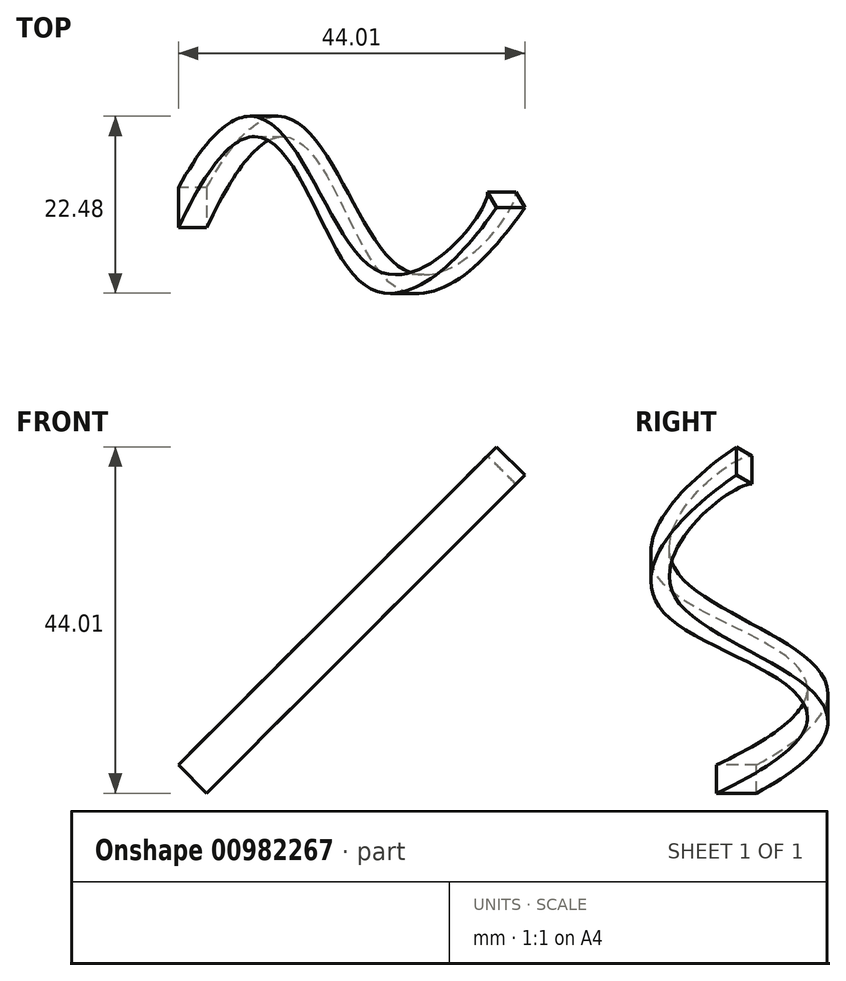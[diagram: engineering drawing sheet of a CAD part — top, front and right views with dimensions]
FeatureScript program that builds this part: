
annotation { "Feature Type Name" : "Feature", "Feature Type Description" : "" }
export const myFeature = defineFeature(function(context is Context, id is Id, definition is map)
    precondition{}
    {
        {
            var Q0;
            Q0=qCreatedBy(makeId("Front.planeOp"),FACE);
            var sketch = newSketch(context, id + "F0", { "sketchPlane" : qUnion([Q0])});
            skLineSegment(sketch, "E0", {"start": v(0, 0) * mm, "end": v(27, 27) * mm, "construction": true});
            skSolve(sketch);
        }
        {
            var Q0;
            Q0=qCreatedBy(makeId("Top.planeOp"),FACE);
            var Q1;
            Q1=sQuery(id+"F0.wireOp",EDGE,"E0");
            cPlane(context, id + "F1", {"entities" : qUnion([Q0, Q1]), "cplaneType" : CPlaneType.LINE_ANGLE, "offset" : 25.4 * mm, "angle" : 0 * degree, "width" : 152.4 * mm, "height" : 152.4 * mm});
        }
        {
            var Q0;
            Q0=qCreatedBy(id+"F1.planeOp",FACE);
            var sketch = newSketch(context, id + "F2", { "sketchPlane" : qUnion([Q0])});
            skFitSpline(sketch, "E1", {"points": [v(0, 0) * mm, v(-10.28, 35.04) * mm, v(-0.6, 55.53) * mm, v(0, 55.03) * mm], "startDerivative": vector(135.73, 105.75) * mm, "endDerivative": vector(-1.05, 1.8) * mm});
            skLineSegment(sketch, "E2", {"start": v(0, 0) * mm, "end": v(-5.08, 0) * mm});
            skPoint(sketch, "E3.2.internal.snap0", {"position": v(-2.54, 0) * mm});
            skFitSpline(sketch, "E3", {"points": [v(-5.08, 0) * mm, v(-11.15, 31.53) * mm, v(-2.54, 57.16) * mm], "startDerivative": vector(149.51, 99.55) * mm, "endDerivative": vector(40.27, 38.87) * mm});
            skLineSegment(sketch, "E4", {"start": v(-0.6, 55.53) * mm, "end": v(-2.54, 57.16) * mm});
            skSolve(sketch);
        }
        {
            var Q0;
            Q0 = qSketchRegion(id + "F2", true);
            extrude(context, id + "F3", {"entities" : qUnion([Q0]), "depth" : 5.08 * mm, "offsetDistance" : 25.4 * mm});
        }
    });
